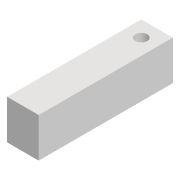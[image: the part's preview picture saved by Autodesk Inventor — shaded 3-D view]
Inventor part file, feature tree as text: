
AUTODESK INVENTOR PART (.ipt)
format: ipt  version: 2022 (Build 260153000, 153)  size: 85,504 bytes
history: native  units: mm
features: extrude x1, sketch x1
ambient origin geometry x8: Origin, YZ Plane, XZ Plane, XY Plane, X Axis, Y Axis, Z Axis, Center Point
bodies: Solid1 (feature_tree)
feature tree (2):
  extrude  "Extrusion1"  Depth=10.0mm
  sketch  "Sketch1"  dims[d0=3.0mm d1=4.0mm d2=30.0mm d3=4.0mm d4=4.0mm d5=10.0mm d6=0.0mm]
